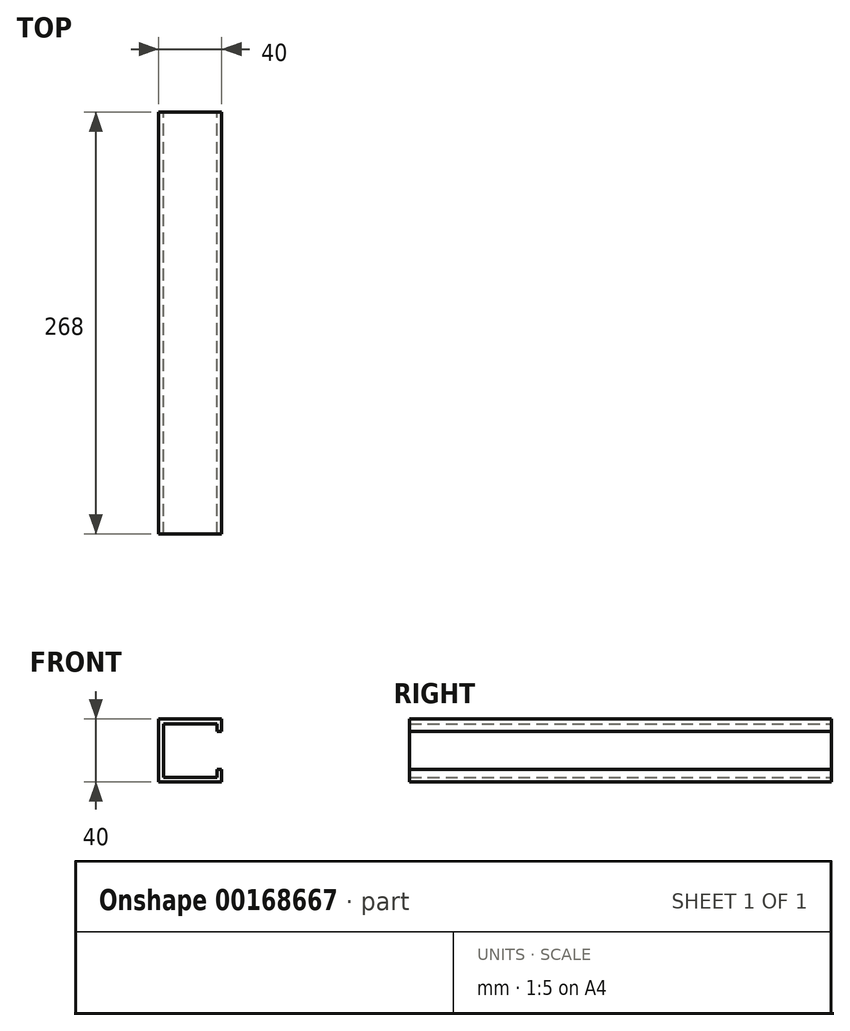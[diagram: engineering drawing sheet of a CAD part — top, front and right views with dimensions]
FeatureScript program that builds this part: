
annotation { "Feature Type Name" : "Feature", "Feature Type Description" : "" }
export const myFeature = defineFeature(function(context is Context, id is Id, definition is map)
    precondition{}
    {
        {
            var Q0;
            Q0=qCreatedBy(makeId("Front.planeOp"),FACE);
            var sketch = newSketch(context, id + "F0", { "sketchPlane" : qUnion([Q0])});
            skLineSegment(sketch, "E0.bottom", {"start": v(20, 20) * mm, "end": v(-20, 20) * mm});
            skLineSegment(sketch, "E0.top", {"start": v(20, -20) * mm, "end": v(-20, -20) * mm});
            skLineSegment(sketch, "E0.right", {"start": v(-20, 20) * mm, "end": v(-20, -20) * mm});
            skPoint(sketch, "E0.middle", {"position": v(0, 0) * mm});
            skLineSegment(sketch, "E1.0", {"start": v(17, -17) * mm, "end": v(-17, -17) * mm});
            skLineSegment(sketch, "E1.1", {"start": v(-17, 17) * mm, "end": v(-17, -17) * mm});
            skLineSegment(sketch, "E1.2", {"start": v(17, 17) * mm, "end": v(-17, 17) * mm});
            skLineSegment(sketch, "E2", {"start": v(17, 17) * mm, "end": v(17, 12) * mm});
            skLineSegment(sketch, "E3", {"start": v(17, 12) * mm, "end": v(20, 12) * mm});
            skLineSegment(sketch, "E4", {"start": v(20, -12) * mm, "end": v(17, -12) * mm});
            skLineSegment(sketch, "E5", {"start": v(17, -12) * mm, "end": v(17, -17) * mm});
            skLineSegment(sketch, "E6", {"start": v(20, 20) * mm, "end": v(20, 12) * mm});
            skLineSegment(sketch, "E7", {"start": v(20, -20) * mm, "end": v(20, -12) * mm});
            skSolve(sketch);
        }
        {
            var Q0;
            Q0=makeQuery(id+"F0.imprint","IMPRINT",FACE,{"disambiguationData":[TD([[makeQuery(id+"F0.imprint","IMPRINT",EDGE,{"derivedFrom":sQuery(id+"F0.wireOp",EDGE,"E0.bottom")}),1.0]])]});
            extrude(context, id + "F1", {"entities" : qUnion([Q0]), "depth" : 268 * mm});
        }
    });
